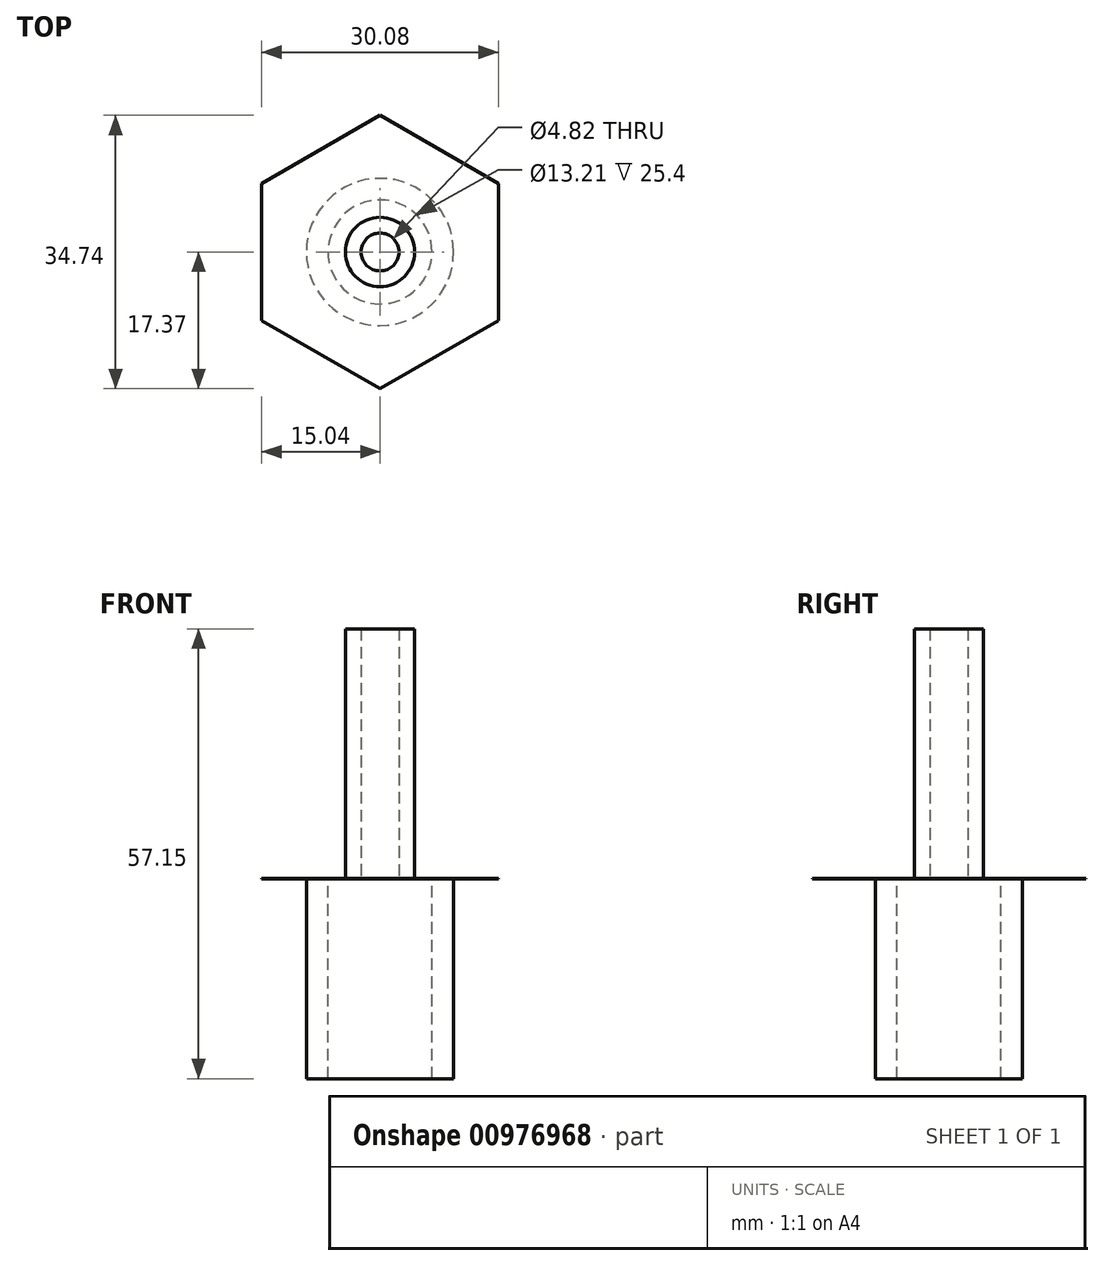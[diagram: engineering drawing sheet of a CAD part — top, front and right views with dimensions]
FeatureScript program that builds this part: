
annotation { "Feature Type Name" : "Feature", "Feature Type Description" : "" }
export const myFeature = defineFeature(function(context is Context, id is Id, definition is map)
    precondition{}
    {
        {
            var Q0;
            Q0=qCreatedBy(makeId("Top.planeOp"),FACE);
            var sketch = newSketch(context, id + "F0", { "sketchPlane" : qUnion([Q0])});
            skCircle(sketch, "E0", {"center": v(0, 0) * mm, "radius": 9.35 * mm});
            skCircle(sketch, "E1.cCircle", {"center": v(0, 0) * mm, "radius": 15.04 * mm, "construction": true});
            skLineSegment(sketch, "E1.0", {"start": v(15.04, 8.68) * mm, "end": v(15.04, -8.68) * mm});
            skLineSegment(sketch, "E1.1", {"start": v(15.04, -8.68) * mm, "end": v(0, -17.37) * mm});
            skLineSegment(sketch, "E1.2", {"start": v(0, -17.37) * mm, "end": v(-15.04, -8.68) * mm});
            skLineSegment(sketch, "E1.3", {"start": v(-15.04, -8.68) * mm, "end": v(-15.04, 8.68) * mm});
            skLineSegment(sketch, "E1.4", {"start": v(-15.04, 8.68) * mm, "end": v(0, 17.37) * mm});
            skLineSegment(sketch, "E1.5", {"start": v(0, 17.37) * mm, "end": v(15.04, 8.68) * mm});
            skPoint(sketch, "E1.0.midPoint", {"position": v(15.04, 0) * mm});
            skCircle(sketch, "E2", {"center": v(0, 0) * mm, "radius": 6.6 * mm});
            skCircle(sketch, "E3", {"center": v(0, 0) * mm, "radius": 2.4 * mm});
            skCircle(sketch, "E4", {"center": v(0, 0) * mm, "radius": 4.4 * mm});
            skSolve(sketch);
        }
        {
            var Q0;
            Q0=makeQuery(id+"F0.imprint","IMPRINT",FACE,{"disambiguationData":[TD([[makeQuery(id+"F0.imprint","IMPRINT",EDGE,{"derivedFrom":sQuery(id+"F0.wireOp",EDGE,"E0")}),-1.0]])]});
            var Q1;
            Q1=makeQuery(id+"F0.imprint","IMPRINT",FACE,{"disambiguationData":[TD([[makeQuery(id+"F0.imprint","IMPRINT",EDGE,{"derivedFrom":sQuery(id+"F0.wireOp",EDGE,"E0")}),1.0]])]});
            var Q2;
            Q2=makeQuery(id+"F0.imprint","IMPRINT",FACE,{"disambiguationData":[TD([[makeQuery(id+"F0.imprint","IMPRINT",EDGE,{"derivedFrom":sQuery(id+"F0.wireOp",EDGE,"E2")}),1.0]])]});
            extrude(context, id + "F1", {"entities" : qUnion([Q0, Q1, Q2]), "depth" : 1 / 101.6 * mm, "offsetDistance" : 25 * mm});
        }
        {
            var Q0;
            Q0=makeQuery(id+"F0.imprint","IMPRINT",FACE,{"disambiguationData":[TD([[makeQuery(id+"F0.imprint","IMPRINT",EDGE,{"derivedFrom":sQuery(id+"F0.wireOp",EDGE,"E3")}),-1.0]])]});
            extrude(context, id + "F2", {"entities" : qUnion([Q0]), "operationType" : NewBodyOperationType.ADD, "depth" : 31.75 * mm, "offsetDistance" : 25.4 * mm});
        }
        {
            var Q0;
            Q0=makeQuery(id+"F0.imprint","IMPRINT",FACE,{"disambiguationData":[TD([[makeQuery(id+"F0.imprint","IMPRINT",EDGE,{"derivedFrom":sQuery(id+"F0.wireOp",EDGE,"E0")}),1.0]])]});
            extrude(context, id + "F3", {"entities" : qUnion([Q0]), "operationType" : NewBodyOperationType.ADD, "oppositeDirection" : true, "depth" : 25.4 * mm, "offsetDistance" : 25.4 * mm});
        }
    });
